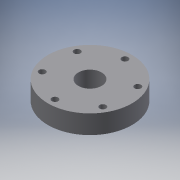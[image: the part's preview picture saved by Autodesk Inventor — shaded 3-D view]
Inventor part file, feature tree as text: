
AUTODESK INVENTOR PART (.ipt)
format: ipt  version: 2016 (Build 200138000, 138)  size: 132,608 bytes
history: native  units: in
note: dims shown in document units (in); Inventor stores cm internally (conversion verified against a paired STEP export)
features: extrude x1, sketch x1
ambient origin geometry x8: Origin, YZ Plane, XZ Plane, XY Plane, X Axis, Y Axis, Z Axis, Center Point
bodies: Body1 (feature_tree)
feature tree (2):
  extrude  "Extrusion2"  Depth=0.503in
  sketch  "Sketch1"  dims[d0=1.875in d1=0.17in d2=0.17in d3=0.17in d4=0.17in d5=0.17in d6=0.17in d7=2.25in d10=0.625in d11=0.503in d12=0.0in]
